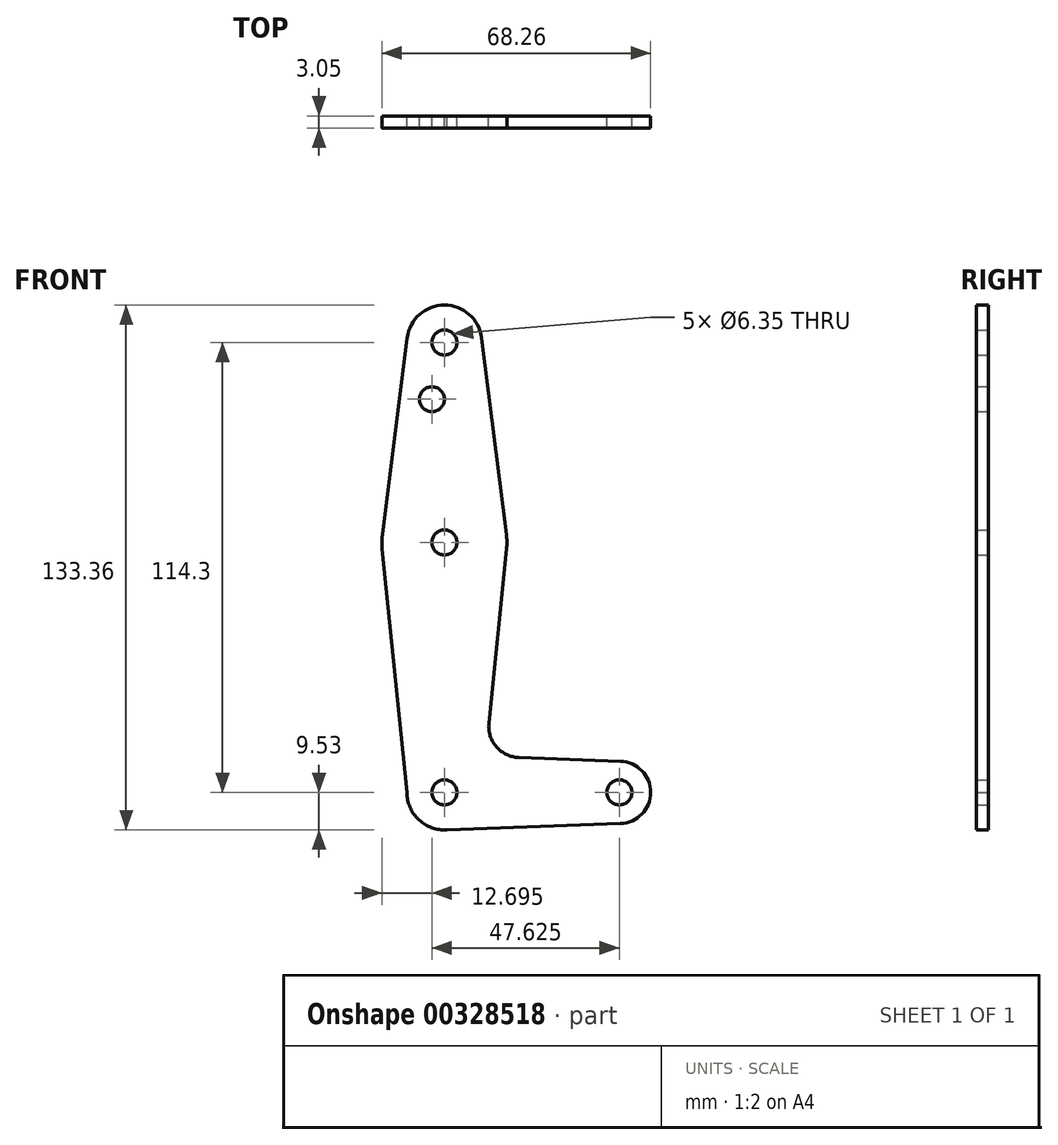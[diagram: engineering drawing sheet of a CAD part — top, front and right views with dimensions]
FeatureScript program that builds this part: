
annotation { "Feature Type Name" : "Feature", "Feature Type Description" : "" }
export const myFeature = defineFeature(function(context is Context, id is Id, definition is map)
    precondition{}
    {
        {
            var Q0;
            Q0=qCreatedBy(makeId("Front.planeOp"),FACE);
            var sketch = newSketch(context, id + "F0", { "sketchPlane" : qUnion([Q0])});
            skLineSegment(sketch, "E0", {"start": v(0, 0) * mm, "end": v(0, 114.3) * mm, "construction": true});
            skLineSegment(sketch, "E1", {"start": v(0, 0) * mm, "end": v(44.45, 0) * mm, "construction": true});
            skCircle(sketch, "E2", {"center": v(0, 114.3) * mm, "radius": 9.53 * mm});
            skCircle(sketch, "E3", {"center": v(0, 0) * mm, "radius": 9.53 * mm});
            skCircle(sketch, "E4", {"center": v(44.45, 0) * mm, "radius": 7.94 * mm});
            skCircle(sketch, "E5", {"center": v(0, 63.5) * mm, "radius": 15.88 * mm});
            skLineSegment(sketch, "E6", {"start": v(11.3, 17.6) * mm, "end": v(15.8, 61.9) * mm});
            skLineSegment(sketch, "E7", {"start": v(-9.52, 0) * mm, "end": v(-15.96, 63.5) * mm});
            skLineSegment(sketch, "E8", {"start": v(18.93, 8.85) * mm, "end": v(44.73, 7.93) * mm});
            skLineSegment(sketch, "E9", {"start": v(-15.75, 65.48) * mm, "end": v(-9.45, 115.5) * mm});
            skLineSegment(sketch, "E10", {"start": v(15.75, 65.48) * mm, "end": v(9.45, 115.5) * mm});
            skLineSegment(sketch, "E11", {"start": v(0, -9.53) * mm, "end": v(44.73, -7.93) * mm});
            skCircle(sketch, "E12", {"center": v(0, 114.3) * mm, "radius": 3.18 * mm});
            skCircle(sketch, "E13", {"center": v(0, 63.5) * mm, "radius": 3.18 * mm});
            skCircle(sketch, "E14", {"center": v(0, 0) * mm, "radius": 3.18 * mm});
            skCircle(sketch, "E15", {"center": v(44.45, 0) * mm, "radius": 3.18 * mm});
            skCircle(sketch, "E16", {"center": v(-3.18, 99.89) * mm, "radius": 3.18 * mm});
            skArc(sketch, "E17.filletArc", {"start": v(11.3, 17.6) * mm, "mid": v(13.22, 11.57) * mm, "end": v(18.93, 8.85) * mm});
            skSolve(sketch);
        }
        {
            var Q0;
            Q0 = qSketchRegion(id + "F0", true);
            extrude(context, id + "F1", {"entities" : qUnion([Q0]), "depth" : 3.05 * mm});
        }
    });
